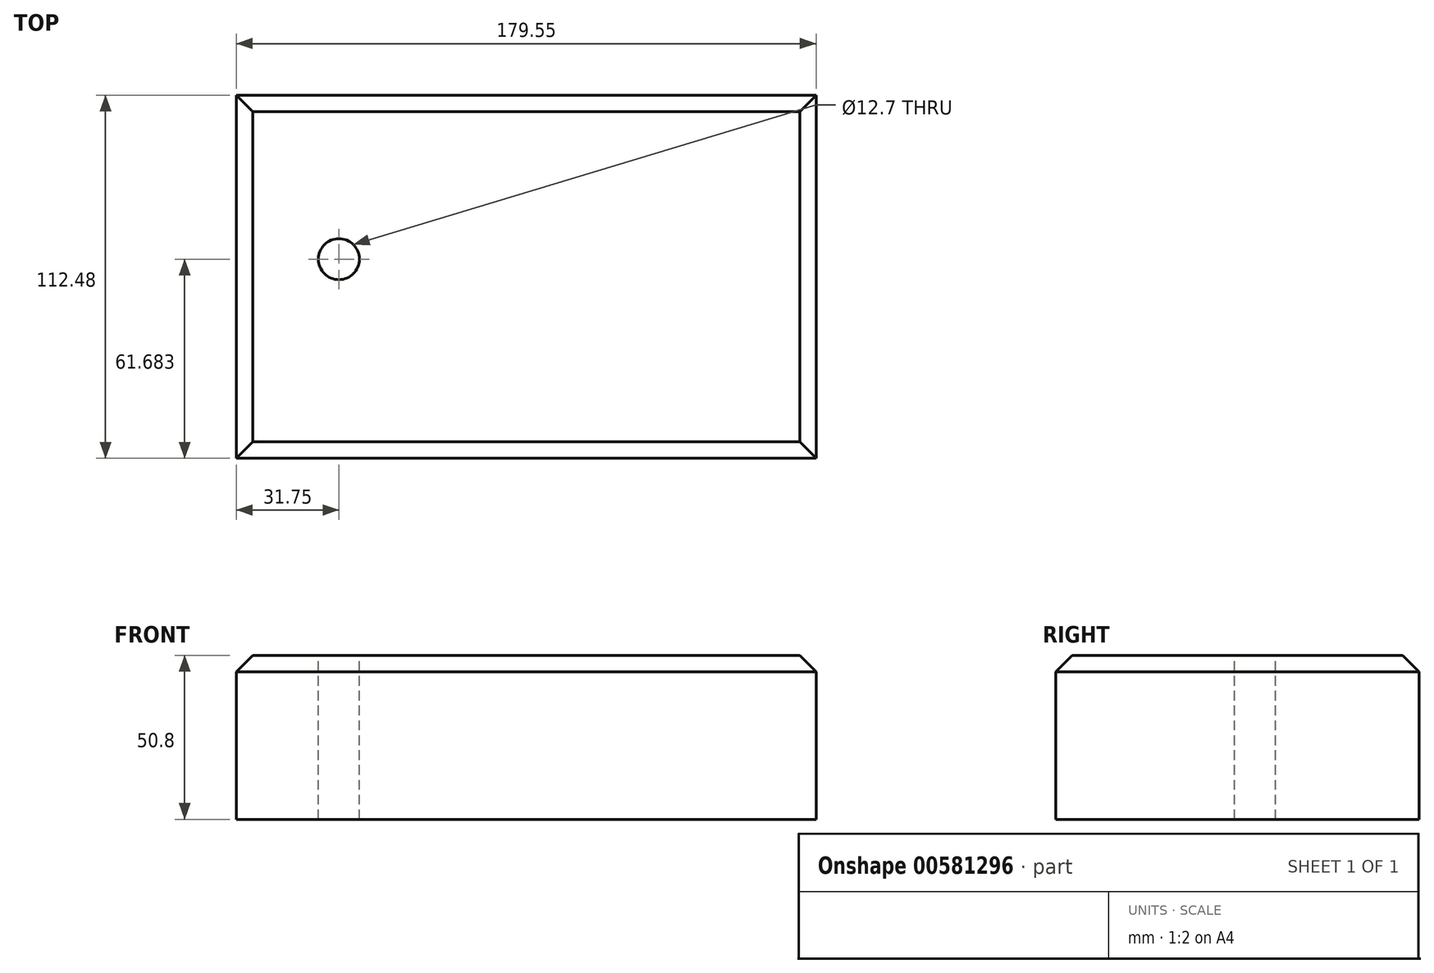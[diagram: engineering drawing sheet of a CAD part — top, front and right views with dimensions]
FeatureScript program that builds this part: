
annotation { "Feature Type Name" : "Feature", "Feature Type Description" : "" }
export const myFeature = defineFeature(function(context is Context, id is Id, definition is map)
    precondition{}
    {
        {
            var Q0;
            Q0=qCreatedBy(makeId("Top.planeOp"),FACE);
            var sketch = newSketch(context, id + "F0", { "sketchPlane" : qUnion([Q0])});
            skLineSegment(sketch, "E0.bottom", {"start": v(-133.28, 67.05) * mm, "end": v(46.27, 67.05) * mm});
            skLineSegment(sketch, "E0.top", {"start": v(-133.28, -45.43) * mm, "end": v(46.27, -45.43) * mm});
            skLineSegment(sketch, "E0.left", {"start": v(-133.28, 67.05) * mm, "end": v(-133.28, -45.43) * mm});
            skLineSegment(sketch, "E0.right", {"start": v(46.27, 67.05) * mm, "end": v(46.27, -45.43) * mm});
            skSolve(sketch);
        }
        {
            var Q0;
            Q0 = qSketchRegion(id + "F0", true);
            extrude(context, id + "F1", {"entities" : qUnion([Q0]), "depth" : 50.8 * mm, "offsetDistance" : 25.4 * mm});
        }
        {
            var Q0;
            Q0=makeQuery(id+"F1.opExtrude","CAP_FACE",FACE,{"disambiguationData":[OSD([sQuery(id+"F0.wireOp",EDGE,"E0.bottom"),sQuery(id+"F0.wireOp",EDGE,"E0.top"),sQuery(id+"F0.wireOp",EDGE,"E0.left"),sQuery(id+"F0.wireOp",EDGE,"E0.right")])],"isStart":false});
            var sketch = newSketch(context, id + "F2", { "sketchPlane" : qUnion([Q0])});
            skPoint(sketch, "E1", {"position": v(-101.53, 16.25) * mm});
            skSolve(sketch);
        }
        {
            var Q0;
            Q0=sQuery(id+"F2.wireOp",VERTEX,"E1");
            var Q1;
            Q1=makeQuery(id+"F1.opExtrude","SWEPT_BODY",BODY,{"disambiguationData":[OSD([sQuery(id+"F0.wireOp",EDGE,"E0.bottom"),sQuery(id+"F0.wireOp",EDGE,"E0.top"),sQuery(id+"F0.wireOp",EDGE,"E0.left"),sQuery(id+"F0.wireOp",EDGE,"E0.right")])]});
            hole(context, id + "F3", {"style" : HoleStyle.SIMPLE, "endStyle" : HoleEndStyle.THROUGH, "holeDiameter" : 12.7 * mm, "majorDiameter" : 6.35 * mm, "isTappedThrough" : true, "tappedDepth" : 12.7 * mm, "tapClearance" : 3, "locations" : qUnion([Q0]), "scope" : qUnion([Q1])});
        }
        {
            var Q0;
            Q0=makeQuery(id+"F1.opExtrude","CAP_EDGE",EDGE,{"disambiguationData":[OSD([sQuery(id+"F0.wireOp",EDGE,"E0.top")])],"isStart":false});
            chamfer(context, id + "F4", {"entities" : qUnion([Q0]), "width" : 5.08 * mm, "tangentPropagation" : true});
        }
        {
            var Q0;
            Q0=makeQuery(id+"F1.opExtrude","CAP_EDGE",EDGE,{"disambiguationData":[OSD([sQuery(id+"F0.wireOp",EDGE,"E0.right")])],"isStart":false});
            var Q1;
            Q1=makeQuery(id+"F1.opExtrude","CAP_EDGE",EDGE,{"disambiguationData":[OSD([sQuery(id+"F0.wireOp",EDGE,"E0.bottom")])],"isStart":false});
            var Q2;
            Q2=makeQuery(id+"F1.opExtrude","CAP_EDGE",EDGE,{"disambiguationData":[OSD([sQuery(id+"F0.wireOp",EDGE,"E0.left")])],"isStart":false});
            chamfer(context, id + "F5", {"entities" : qUnion([Q0, Q1, Q2]), "width" : 5.08 * mm, "tangentPropagation" : true});
        }
    });
